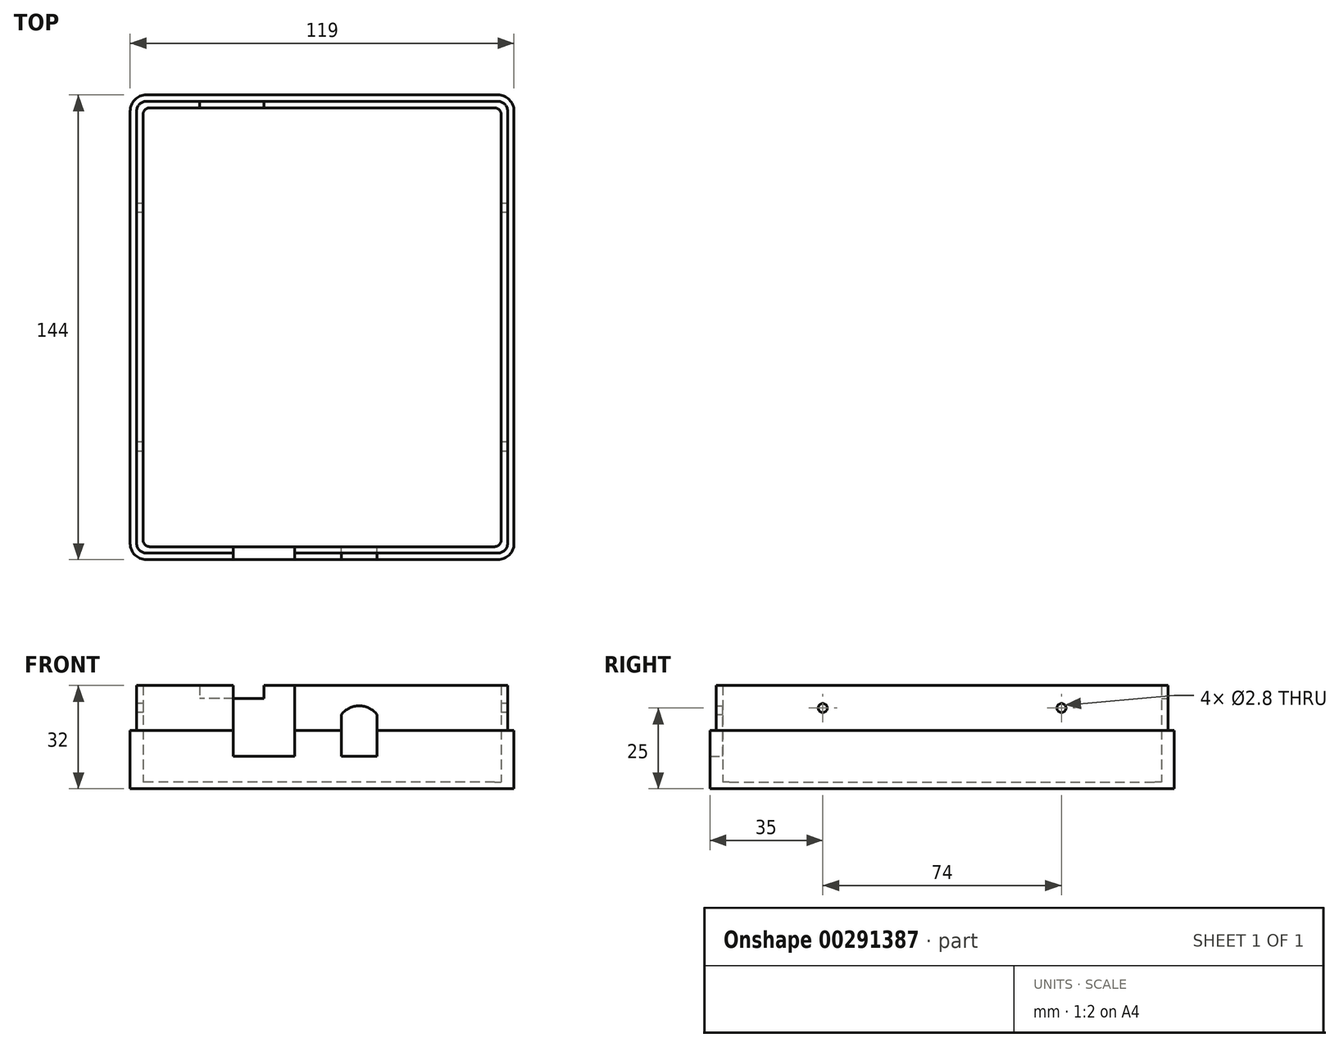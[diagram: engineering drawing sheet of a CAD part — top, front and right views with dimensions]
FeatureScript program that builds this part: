
annotation { "Feature Type Name" : "Feature", "Feature Type Description" : "" }
export const myFeature = defineFeature(function(context is Context, id is Id, definition is map)
    precondition{}
    {
        {
            var Q0;
            Q0=qCreatedBy(makeId("Top.planeOp"),FACE);
            var sketch = newSketch(context, id + "F0", { "sketchPlane" : qUnion([Q0])});
            skLineSegment(sketch, "E0.bottom", {"start": v(57.5, -70) * mm, "end": v(-57.5, -70) * mm});
            skLineSegment(sketch, "E0.top", {"start": v(57.5, 70) * mm, "end": v(-57.5, 70) * mm});
            skLineSegment(sketch, "E0.left", {"start": v(57.5, -70) * mm, "end": v(57.5, 70) * mm});
            skLineSegment(sketch, "E0.right", {"start": v(-57.5, -70) * mm, "end": v(-57.5, 70) * mm});
            skPoint(sketch, "E0.middle", {"position": v(0, 0) * mm});
            skSolve(sketch);
        }
        {
            var Q0;
            Q0=qSketchRegion(id+"F0",true);
            extrude(context, id + "F1", {"entities" : qUnion([Q0]), "depth" : 2 * mm});
        }
        {
            var Q0;
            Q0=makeQuery(id+"F1.opExtrude","CAP_FACE",FACE,{"disambiguationData":[OSD([sQuery(id+"F0.wireOp",EDGE,"E0.bottom"),sQuery(id+"F0.wireOp",EDGE,"E0.top"),sQuery(id+"F0.wireOp",EDGE,"E0.left"),sQuery(id+"F0.wireOp",EDGE,"E0.right")])],"isStart":false});
            var sketch = newSketch(context, id + "F2", { "sketchPlane" : qUnion([Q0])});
            skLineSegment(sketch, "E1.bottom", {"start": v(57.5, -70) * mm, "end": v(-57.5, -70) * mm});
            skLineSegment(sketch, "E1.top", {"start": v(57.5, 70) * mm, "end": v(-57.5, 70) * mm});
            skLineSegment(sketch, "E1.left", {"start": v(57.5, -70) * mm, "end": v(57.5, 70) * mm});
            skLineSegment(sketch, "E1.right", {"start": v(-57.5, -70) * mm, "end": v(-57.5, 70) * mm});
            skPoint(sketch, "E1.middle", {"position": v(0, 0) * mm});
            skLineSegment(sketch, "E2.bottom", {"start": v(55.5, -68) * mm, "end": v(-55.5, -68) * mm});
            skLineSegment(sketch, "E2.top", {"start": v(55.5, 68) * mm, "end": v(-55.5, 68) * mm});
            skLineSegment(sketch, "E2.left", {"start": v(55.5, -68) * mm, "end": v(55.5, 68) * mm});
            skLineSegment(sketch, "E2.right", {"start": v(-55.5, -68) * mm, "end": v(-55.5, 68) * mm});
            skSolve(sketch);
        }
        {
            var Q0;
            Q0=qSketchRegion(id+"F2",true);
            extrude(context, id + "F3", {"entities" : qUnion([Q0]), "operationType" : NewBodyOperationType.ADD, "depth" : 30 * mm});
        }
        {
            var Q0;
            Q0=qCreatedBy(makeId("Top.planeOp"),FACE);
            var sketch = newSketch(context, id + "F4", { "sketchPlane" : qUnion([Q0])});
            skLineSegment(sketch, "E3.bottom", {"start": v(59.5, -72) * mm, "end": v(-59.5, -72) * mm});
            skLineSegment(sketch, "E3.top", {"start": v(59.5, 72) * mm, "end": v(-59.5, 72) * mm});
            skLineSegment(sketch, "E3.left", {"start": v(59.5, -72) * mm, "end": v(59.5, 72) * mm});
            skLineSegment(sketch, "E3.right", {"start": v(-59.5, -72) * mm, "end": v(-59.5, 72) * mm});
            skPoint(sketch, "E3.middle", {"position": v(0, 0) * mm});
            skLineSegment(sketch, "E4.bottom", {"start": v(57.5, -70) * mm, "end": v(-57.5, -70) * mm});
            skLineSegment(sketch, "E4.top", {"start": v(57.5, 70) * mm, "end": v(-57.5, 70) * mm});
            skLineSegment(sketch, "E4.left", {"start": v(57.5, -70) * mm, "end": v(57.5, 70) * mm});
            skLineSegment(sketch, "E4.right", {"start": v(-57.5, -70) * mm, "end": v(-57.5, 70) * mm});
            skSolve(sketch);
        }
        {
            var Q0;
            Q0 = qSketchRegion(id + "F4", true);
            extrude(context, id + "F5", {"entities" : qUnion([Q0]), "operationType" : NewBodyOperationType.ADD, "depth" : 18 * mm});
        }
        {
            var Q0;
            Q0=makeQuery(id+"F3.opExtrude","SWEPT_FACE",FACE,{"disambiguationData":[OSD([sQuery(id+"F2.wireOp",EDGE,"E2.bottom")])]});
            var sketch = newSketch(context, id + "F6", { "sketchPlane" : qUnion([Q0])});
            skLineSegment(sketch, "E5.bottom", {"start": v(8.5, 42) * mm, "end": v(27.5, 42) * mm});
            skLineSegment(sketch, "E5.top", {"start": v(8.5, 10) * mm, "end": v(27.5, 10) * mm});
            skLineSegment(sketch, "E5.left", {"start": v(8.5, 42) * mm, "end": v(8.5, 10) * mm});
            skLineSegment(sketch, "E5.right", {"start": v(27.5, 42) * mm, "end": v(27.5, 10) * mm});
            skLineSegment(sketch, "E6.bottom", {"start": v(-6, 23) * mm, "end": v(-17, 23) * mm, "construction": true});
            skLineSegment(sketch, "E6.top", {"start": v(-6, 10) * mm, "end": v(-17, 10) * mm});
            skLineSegment(sketch, "E6.left", {"start": v(-6, 23) * mm, "end": v(-6, 10) * mm});
            skLineSegment(sketch, "E6.right", {"start": v(-17, 23) * mm, "end": v(-17, 10) * mm});
            skLineSegment(sketch, "E7.bottom", {"start": v(27.5, 42) * mm, "end": v(8.5, 42) * mm});
            skLineSegment(sketch, "E7.top", {"start": v(27.5, 45.22) * mm, "end": v(8.5, 45.22) * mm});
            skLineSegment(sketch, "E7.left", {"start": v(27.5, 42) * mm, "end": v(27.5, 45.22) * mm});
            skLineSegment(sketch, "E7.right", {"start": v(8.5, 42) * mm, "end": v(8.5, 45.22) * mm});
            skArc(sketch, "E8", {"start": v(-6, 23) * mm, "mid": v(-11.5, 25.67) * mm, "end": v(-17, 23) * mm});
            skSolve(sketch);
        }
        {
            var Q0;
            Q0=qSketchRegion(id+"F6",true);
            extrude(context, id + "F7", {"entities" : qUnion([Q0]), "operationType" : NewBodyOperationType.REMOVE, "endBound" : BoundingType.SYMMETRIC, "oppositeDirection" : true, "depth" : 10 * mm});
        }
        {
            var Q0;
            Q0=makeQuery(id+"F3.boolean.opBoolean","MERGE",FACE,{"derivedFrom":[makeQuery(id+"F1.opExtrude","SWEPT_FACE",FACE,{"disambiguationData":[OSD([sQuery(id+"F0.wireOp",EDGE,"E0.top")])]}),makeQuery(id+"F3.opExtrude","SWEPT_FACE",FACE,{"disambiguationData":[OSD([sQuery(id+"F2.wireOp",EDGE,"E1.top")])]})]});
            var sketch = newSketch(context, id + "F8", { "sketchPlane" : qUnion([Q0])});
            skLineSegment(sketch, "E9.bottom", {"start": v(18, 39) * mm, "end": v(38, 39) * mm});
            skLineSegment(sketch, "E9.top", {"start": v(18, 28) * mm, "end": v(38, 28) * mm});
            skLineSegment(sketch, "E9.left", {"start": v(18, 39) * mm, "end": v(18, 28) * mm});
            skLineSegment(sketch, "E9.right", {"start": v(38, 39) * mm, "end": v(38, 28) * mm});
            skSolve(sketch);
        }
        {
            var Q0;
            Q0=qSketchRegion(id+"F8",true);
            extrude(context, id + "F9", {"entities" : qUnion([Q0]), "operationType" : NewBodyOperationType.REMOVE, "oppositeDirection" : true, "depth" : 2 * mm});
        }
        {
            var Q0;
            Q0=makeQuery(id+"F5.opExtrude","SWEPT_EDGE",EDGE,{"disambiguationData":[OSD([sQuery(id+"F4.wireOp",EDGE,"E3.bottom"),sQuery(id+"F4.wireOp",EDGE,"E3.right")])]});
            var Q1;
            Q1=makeQuery(id+"F5.opExtrude","SWEPT_EDGE",EDGE,{"disambiguationData":[OSD([sQuery(id+"F4.wireOp",EDGE,"E3.bottom"),sQuery(id+"F4.wireOp",EDGE,"E3.left")])]});
            var Q2;
            Q2=makeQuery(id+"F5.opExtrude","SWEPT_EDGE",EDGE,{"disambiguationData":[OSD([sQuery(id+"F4.wireOp",EDGE,"E3.top"),sQuery(id+"F4.wireOp",EDGE,"E3.right")])]});
            var Q3;
            Q3=makeQuery(id+"F5.opExtrude","SWEPT_EDGE",EDGE,{"disambiguationData":[OSD([sQuery(id+"F4.wireOp",EDGE,"E3.top"),sQuery(id+"F4.wireOp",EDGE,"E3.left")])]});
            fillet(context, id + "F10", {"entities" : qUnion([Q0, Q1, Q2, Q3]), "radius" : 5 * mm, "tangentPropagation" : true, "allowEdgeOverflow" : false});
        }
        {
            var Q0;
            Q0=makeQuery(id+"F3.boolean.opBoolean","MERGE",EDGE,{"derivedFrom":[makeQuery(id+"F1.opExtrude","SWEPT_EDGE",EDGE,{"disambiguationData":[OSD([sQuery(id+"F0.wireOp",EDGE,"E0.bottom"),sQuery(id+"F0.wireOp",EDGE,"E0.right")])]}),makeQuery(id+"F3.opExtrude","SWEPT_EDGE",EDGE,{"disambiguationData":[OSD([sQuery(id+"F2.wireOp",EDGE,"E1.bottom"),sQuery(id+"F2.wireOp",EDGE,"E1.right")])]})]});
            var Q1;
            Q1=makeQuery(id+"F3.boolean.opBoolean","MERGE",EDGE,{"derivedFrom":[makeQuery(id+"F1.opExtrude","SWEPT_EDGE",EDGE,{"disambiguationData":[OSD([sQuery(id+"F0.wireOp",EDGE,"E0.bottom"),sQuery(id+"F0.wireOp",EDGE,"E0.left")])]}),makeQuery(id+"F3.opExtrude","SWEPT_EDGE",EDGE,{"disambiguationData":[OSD([sQuery(id+"F2.wireOp",EDGE,"E1.bottom"),sQuery(id+"F2.wireOp",EDGE,"E1.left")])]})]});
            var Q2;
            Q2=makeQuery(id+"F3.boolean.opBoolean","MERGE",EDGE,{"derivedFrom":[makeQuery(id+"F1.opExtrude","SWEPT_EDGE",EDGE,{"disambiguationData":[OSD([sQuery(id+"F0.wireOp",EDGE,"E0.top"),sQuery(id+"F0.wireOp",EDGE,"E0.left")])]}),makeQuery(id+"F3.opExtrude","SWEPT_EDGE",EDGE,{"disambiguationData":[OSD([sQuery(id+"F2.wireOp",EDGE,"E1.top"),sQuery(id+"F2.wireOp",EDGE,"E1.left")])]})]});
            var Q3;
            Q3=makeQuery(id+"F3.boolean.opBoolean","MERGE",EDGE,{"derivedFrom":[makeQuery(id+"F1.opExtrude","SWEPT_EDGE",EDGE,{"disambiguationData":[OSD([sQuery(id+"F0.wireOp",EDGE,"E0.top"),sQuery(id+"F0.wireOp",EDGE,"E0.right")])]}),makeQuery(id+"F3.opExtrude","SWEPT_EDGE",EDGE,{"disambiguationData":[OSD([sQuery(id+"F2.wireOp",EDGE,"E1.top"),sQuery(id+"F2.wireOp",EDGE,"E1.right")])]})]});
            fillet(context, id + "F11", {"entities" : qUnion([Q0, Q1, Q2, Q3]), "radius" : 3 * mm, "tangentPropagation" : true, "allowEdgeOverflow" : false});
        }
        {
            var Q0;
            Q0=makeQuery(id+"F3.opExtrude","SWEPT_EDGE",EDGE,{"disambiguationData":[OSD([sQuery(id+"F2.wireOp",EDGE,"E2.bottom"),sQuery(id+"F2.wireOp",EDGE,"E2.right")])]});
            var Q1;
            Q1=makeQuery(id+"F3.opExtrude","SWEPT_EDGE",EDGE,{"disambiguationData":[OSD([sQuery(id+"F2.wireOp",EDGE,"E2.bottom"),sQuery(id+"F2.wireOp",EDGE,"E2.left")])]});
            var Q2;
            Q2=makeQuery(id+"F3.opExtrude","SWEPT_EDGE",EDGE,{"disambiguationData":[OSD([sQuery(id+"F2.wireOp",EDGE,"E2.top"),sQuery(id+"F2.wireOp",EDGE,"E2.left")])]});
            var Q3;
            Q3=makeQuery(id+"F3.opExtrude","SWEPT_EDGE",EDGE,{"disambiguationData":[OSD([sQuery(id+"F2.wireOp",EDGE,"E2.top"),sQuery(id+"F2.wireOp",EDGE,"E2.right")])]});
            fillet(context, id + "F12", {"entities" : qUnion([Q0, Q1, Q2, Q3]), "radius" : 2 * mm, "tangentPropagation" : true, "allowEdgeOverflow" : false});
        }
        {
            var Q0;
            Q0=makeQuery(id+"F3.boolean.opBoolean","MERGE",FACE,{"derivedFrom":[makeQuery(id+"F1.opExtrude","SWEPT_FACE",FACE,{"disambiguationData":[OSD([sQuery(id+"F0.wireOp",EDGE,"E0.right")])]}),makeQuery(id+"F3.opExtrude","SWEPT_FACE",FACE,{"disambiguationData":[OSD([sQuery(id+"F2.wireOp",EDGE,"E1.right")])]})]});
            var sketch = newSketch(context, id + "F13", { "sketchPlane" : qUnion([Q0])});
            skCircle(sketch, "E10", {"center": v(-37, 25) * mm, "radius": 1.4 * mm});
            skCircle(sketch, "E11", {"center": v(37, 25) * mm, "radius": 1.4 * mm});
            skSolve(sketch);
        }
        {
            var Q0;
            Q0 = qSketchRegion(id + "F13", true);
            extrude(context, id + "F14", {"entities" : qUnion([Q0]), "operationType" : NewBodyOperationType.REMOVE, "endBound" : BoundingType.THROUGH_ALL, "oppositeDirection" : true, "depth" : 25 * mm});
        }
    });
